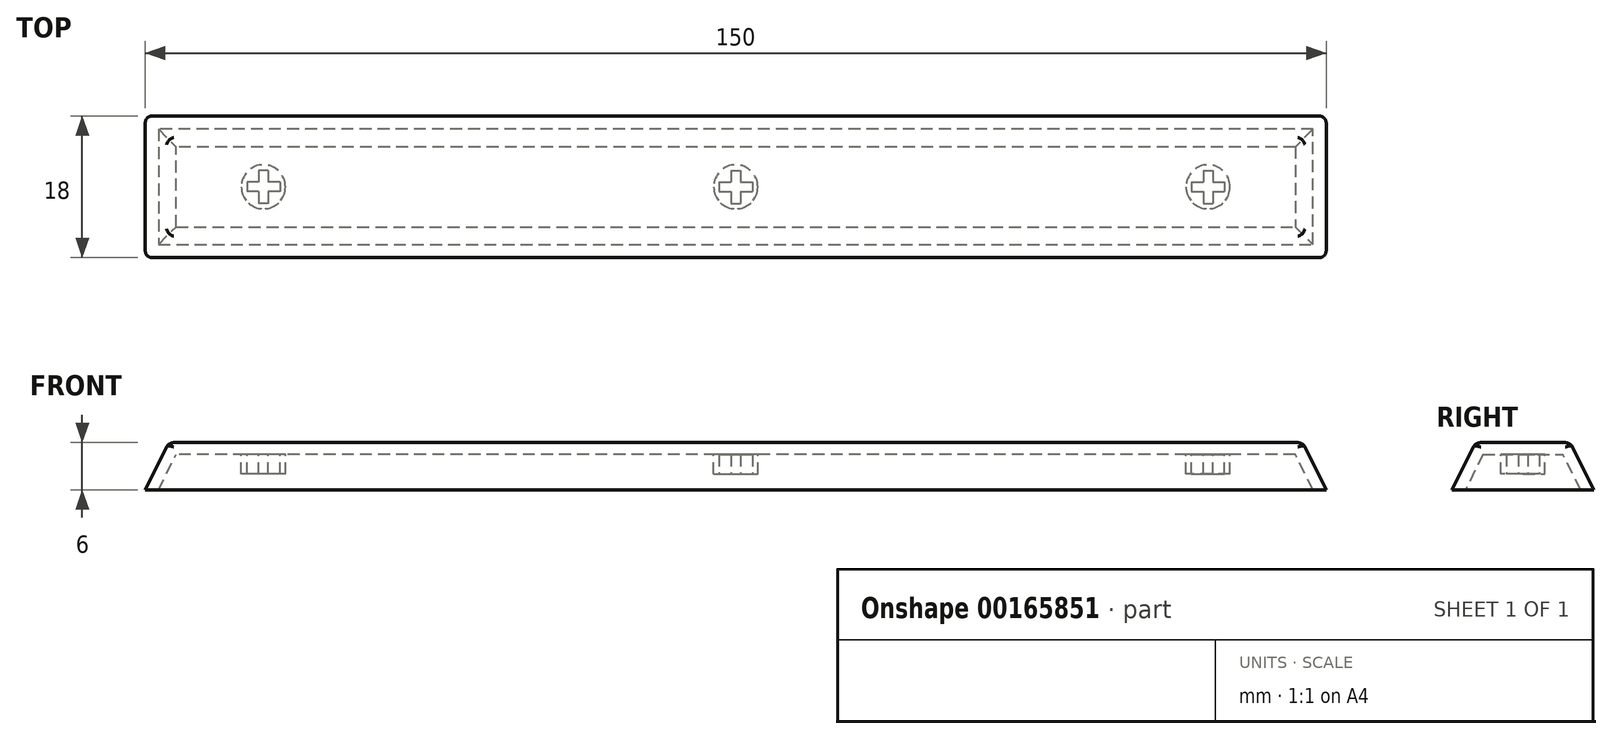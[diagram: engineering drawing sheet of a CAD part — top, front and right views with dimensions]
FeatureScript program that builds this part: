
annotation { "Feature Type Name" : "Feature", "Feature Type Description" : "" }
export const myFeature = defineFeature(function(context is Context, id is Id, definition is map)
    precondition{}
    {
        {
            var Q0;
            Q0=qCreatedBy(makeId("Top.planeOp"),FACE);
            var sketch = newSketch(context, id + "F0", { "sketchPlane" : qUnion([Q0])});
            skLineSegment(sketch, "E0.bottom", {"start": v(75, 9) * mm, "end": v(-75, 9) * mm});
            skLineSegment(sketch, "E0.top", {"start": v(75, -9) * mm, "end": v(-75, -9) * mm});
            skLineSegment(sketch, "E0.left", {"start": v(75, 9) * mm, "end": v(75, -9) * mm});
            skLineSegment(sketch, "E0.right", {"start": v(-75, 9) * mm, "end": v(-75, -9) * mm});
            skPoint(sketch, "E0.middle", {"position": v(0, 0) * mm});
            skSolve(sketch);
        }
        {
            var Q0;
            Q0 = qSketchRegion(id + "F0", true);
            extrude(context, id + "F1", {"entities" : qUnion([Q0]), "depth" : 6 * mm});
        }
        {
            var Q0;
            Q0=makeQuery(id+"F1.opExtrude","CAP_FACE",FACE,{"disambiguationData":[OSD([sQuery(id+"F0.wireOp",EDGE,"E0.bottom"),sQuery(id+"F0.wireOp",EDGE,"E0.top"),sQuery(id+"F0.wireOp",EDGE,"E0.left"),sQuery(id+"F0.wireOp",EDGE,"E0.right")])],"isStart":false});
            chamfer(context, id + "F2", {"entities" : qUnion([Q0]), "chamferType" : ChamferType.TWO_OFFSETS, "width1" : 3 * mm, "oppositeDirection" : false, "width2" : 6 * mm, "tangentPropagation" : true});
        }
        {
            var Q0;
            Q0=makeQuery(id+"F2.opChamfer","BLEND_EDGE",EDGE,{"blendedFrom":[makeQuery(id+"F1.opExtrude","CAP_EDGE",EDGE,{"disambiguationData":[OSD([sQuery(id+"F0.wireOp",EDGE,"E0.bottom")])],"isStart":false}),makeQuery(id+"F1.opExtrude","CAP_EDGE",EDGE,{"disambiguationData":[OSD([sQuery(id+"F0.wireOp",EDGE,"E0.right")])],"isStart":false})],"blendedInto":[]});
            var Q1;
            Q1=makeQuery(id+"F2.opChamfer","BLEND_EDGE",EDGE,{"blendedFrom":[makeQuery(id+"F1.opExtrude","CAP_EDGE",EDGE,{"disambiguationData":[OSD([sQuery(id+"F0.wireOp",EDGE,"E0.top")])],"isStart":false}),makeQuery(id+"F1.opExtrude","CAP_EDGE",EDGE,{"disambiguationData":[OSD([sQuery(id+"F0.wireOp",EDGE,"E0.right")])],"isStart":false})],"blendedInto":[]});
            var Q2;
            Q2=makeQuery(id+"F1.opExtrude","CAP_FACE",FACE,{"disambiguationData":[OSD([sQuery(id+"F0.wireOp",EDGE,"E0.bottom"),sQuery(id+"F0.wireOp",EDGE,"E0.top"),sQuery(id+"F0.wireOp",EDGE,"E0.left"),sQuery(id+"F0.wireOp",EDGE,"E0.right")])],"isStart":false});
            var Q3;
            Q3=makeQuery(id+"F2.opChamfer","BLEND_EDGE",EDGE,{"blendedFrom":[makeQuery(id+"F1.opExtrude","CAP_EDGE",EDGE,{"disambiguationData":[OSD([sQuery(id+"F0.wireOp",EDGE,"E0.bottom")])],"isStart":false}),makeQuery(id+"F1.opExtrude","CAP_EDGE",EDGE,{"disambiguationData":[OSD([sQuery(id+"F0.wireOp",EDGE,"E0.left")])],"isStart":false})],"blendedInto":[]});
            var Q4;
            Q4=makeQuery(id+"F2.opChamfer","BLEND_EDGE",EDGE,{"blendedFrom":[makeQuery(id+"F1.opExtrude","CAP_EDGE",EDGE,{"disambiguationData":[OSD([sQuery(id+"F0.wireOp",EDGE,"E0.top")])],"isStart":false}),makeQuery(id+"F1.opExtrude","CAP_EDGE",EDGE,{"disambiguationData":[OSD([sQuery(id+"F0.wireOp",EDGE,"E0.left")])],"isStart":false})],"blendedInto":[]});
            fillet(context, id + "F3", {"entities" : qUnion([Q0, Q1, Q2, Q3, Q4]), "radius" : 1 * mm, "tangentPropagation" : true, "allowEdgeOverflow" : false});
        }
        {
            var Q0;
            Q0=makeQuery(id+"F1.opExtrude","CAP_FACE",FACE,{"disambiguationData":[OSD([sQuery(id+"F0.wireOp",EDGE,"E0.bottom"),sQuery(id+"F0.wireOp",EDGE,"E0.top"),sQuery(id+"F0.wireOp",EDGE,"E0.left"),sQuery(id+"F0.wireOp",EDGE,"E0.right")])],"isStart":true});
            shell(context, id + "F4", {"entities" : qUnion([Q0]), "thickness" : 1.5 * mm});
        }
        {
            var Q0;
            Q0=makeQuery(id+"F4.opShell","OFFSET_FACE",FACE,{"disambiguationData":[OSD([sQuery(id+"F0.wireOp",EDGE,"E0.bottom"),sQuery(id+"F0.wireOp",EDGE,"E0.top"),sQuery(id+"F0.wireOp",EDGE,"E0.left"),sQuery(id+"F0.wireOp",EDGE,"E0.right")])]});
            var sketch = newSketch(context, id + "F5", { "sketchPlane" : qUnion([Q0])});
            skCircle(sketch, "E1", {"center": v(0, 0) * mm, "radius": 2.8 * mm});
            skSolve(sketch);
        }
        {
            var Q0;
            Q0 = qSketchRegion(id + "F5", true);
            extrude(context, id + "F6", {"entities" : qUnion([Q0]), "operationType" : NewBodyOperationType.ADD, "depth" : 2.5 * mm});
        }
        {
            var Q0;
            Q0=makeQuery(id+"F6.opExtrude","CAP_FACE",FACE,{"disambiguationData":[OSD([sQuery(id+"F5.wireOp",EDGE,"E1")])],"isStart":false});
            var sketch = newSketch(context, id + "F7", { "sketchPlane" : qUnion([Q0])});
            skLineSegment(sketch, "E2.bottom", {"start": v(-2.1, -0.6) * mm, "end": v(2.1, -0.6) * mm});
            skLineSegment(sketch, "E2.top", {"start": v(-2.1, 0.6) * mm, "end": v(2.1, 0.6) * mm});
            skLineSegment(sketch, "E2.left", {"start": v(-2.1, -0.6) * mm, "end": v(-2.1, 0.6) * mm});
            skLineSegment(sketch, "E2.right", {"start": v(2.1, -0.6) * mm, "end": v(2.1, 0.6) * mm});
            skPoint(sketch, "E2.middle", {"position": v(0, 0) * mm});
            skLineSegment(sketch, "E3.bottom", {"start": v(-0.6, -2.1) * mm, "end": v(0.6, -2.1) * mm});
            skLineSegment(sketch, "E3.top", {"start": v(-0.6, 2.1) * mm, "end": v(0.6, 2.1) * mm});
            skLineSegment(sketch, "E3.left", {"start": v(-0.6, -2.1) * mm, "end": v(-0.6, 2.1) * mm});
            skLineSegment(sketch, "E3.right", {"start": v(0.6, -2.1) * mm, "end": v(0.6, 2.1) * mm});
            skSolve(sketch);
        }
        {
            var Q0;
            Q0 = qSketchRegion(id + "F7", true);
            extrude(context, id + "F8", {"entities" : qUnion([Q0]), "operationType" : NewBodyOperationType.REMOVE, "oppositeDirection" : true, "depth" : 2.5 * mm});
        }
        {
            var Q0;
            Q0=makeQuery(id+"F4.opShell","OFFSET_FACE",FACE,{"disambiguationData":[OSD([sQuery(id+"F0.wireOp",EDGE,"E0.bottom"),sQuery(id+"F0.wireOp",EDGE,"E0.top"),sQuery(id+"F0.wireOp",EDGE,"E0.left"),sQuery(id+"F0.wireOp",EDGE,"E0.right")])]});
            var sketch = newSketch(context, id + "F9", { "sketchPlane" : qUnion([Q0])});
            skLineSegment(sketch, "E4", {"start": v(0, 0) * mm, "end": v(60, 0) * mm});
            skCircle(sketch, "E5", {"center": v(60, 0) * mm, "radius": 2.8 * mm});
            skLineSegment(sketch, "E6.bottom", {"start": v(59.4, -2.1) * mm, "end": v(60.6, -2.1) * mm});
            skLineSegment(sketch, "E6.top", {"start": v(59.4, 2.1) * mm, "end": v(60.6, 2.1) * mm});
            skLineSegment(sketch, "E6.left", {"start": v(59.4, -2.1) * mm, "end": v(59.4, 2.1) * mm});
            skLineSegment(sketch, "E6.right", {"start": v(60.6, -2.1) * mm, "end": v(60.6, 2.1) * mm});
            skLineSegment(sketch, "E7.bottom", {"start": v(57.9, -0.6) * mm, "end": v(62.1, -0.6) * mm});
            skLineSegment(sketch, "E7.top", {"start": v(57.9, 0.6) * mm, "end": v(62.1, 0.6) * mm});
            skLineSegment(sketch, "E7.left", {"start": v(57.9, -0.6) * mm, "end": v(57.9, 0.6) * mm});
            skLineSegment(sketch, "E7.right", {"start": v(62.1, -0.6) * mm, "end": v(62.1, 0.6) * mm});
            skLineSegment(sketch, "E8", {"start": v(0, -5.07) * mm, "end": v(0, -3.72) * mm});
            skLineSegment(sketch, "E9.MirrorCS", {"start": v(-59.4, -2.1) * mm, "end": v(-60.6, -2.1) * mm});
            skLineSegment(sketch, "E10.MirrorCS", {"start": v(-59.4, 2.1) * mm, "end": v(-60.6, 2.1) * mm});
            skLineSegment(sketch, "E11.MirrorCS", {"start": v(-62.1, -0.6) * mm, "end": v(-62.1, 0.6) * mm});
            skLineSegment(sketch, "E12.MirrorCS", {"start": v(-57.9, -0.6) * mm, "end": v(-57.9, 0.6) * mm});
            skPoint(sketch, "E13.MirrorP", {"position": v(-60, 0) * mm});
            skCircle(sketch, "E14.MirrorC", {"center": v(-60, 0) * mm, "radius": 2.8 * mm});
            skLineSegment(sketch, "E15.MirrorCS", {"start": v(-59.4, -2.1) * mm, "end": v(-59.4, 2.1) * mm});
            skLineSegment(sketch, "E16.MirrorCS", {"start": v(-60.6, -2.1) * mm, "end": v(-60.6, 2.1) * mm});
            skLineSegment(sketch, "E17.MirrorCS", {"start": v(-57.9, -0.6) * mm, "end": v(-62.1, -0.6) * mm});
            skLineSegment(sketch, "E18.MirrorCS", {"start": v(-57.9, 0.6) * mm, "end": v(-62.1, 0.6) * mm});
            skSolve(sketch);
        }
        {
            var Q0;
            Q0 = qSketchRegion(id + "F9", true);
            extrude(context, id + "F10", {"entities" : qUnion([Q0]), "operationType" : NewBodyOperationType.ADD, "depth" : 2.5 * mm});
        }
    });
